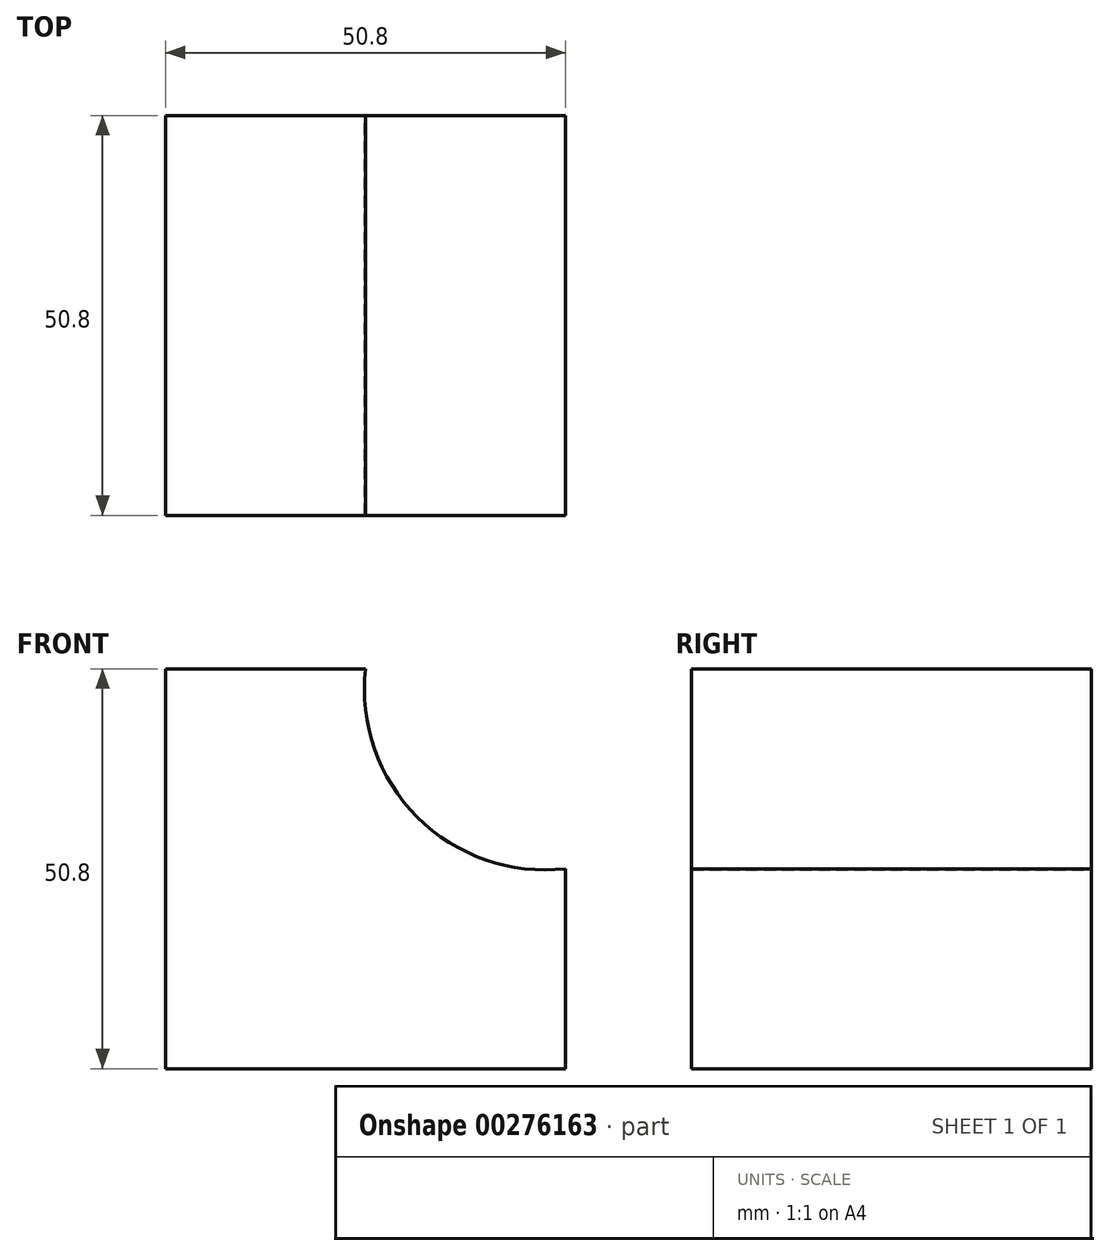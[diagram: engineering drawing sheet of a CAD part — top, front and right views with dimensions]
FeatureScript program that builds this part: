
annotation { "Feature Type Name" : "Feature", "Feature Type Description" : "" }
export const myFeature = defineFeature(function(context is Context, id is Id, definition is map)
    precondition{}
    {
        {
            var Q0;
            Q0=qCreatedBy(makeId("Front.planeOp"),FACE);
            var sketch = newSketch(context, id + "F0", { "sketchPlane" : qUnion([Q0])});
            skLineSegment(sketch, "E0", {"start": v(0, 0) * mm, "end": v(-50.8, 0) * mm});
            skLineSegment(sketch, "E1", {"start": v(-50.8, 0) * mm, "end": v(-50.8, 50.8) * mm});
            skLineSegment(sketch, "E2", {"start": v(-50.8, 50.8) * mm, "end": v(-25.4, 50.8) * mm});
            skLineSegment(sketch, "E3", {"start": v(0, 0) * mm, "end": v(0, 25.4) * mm});
            skArc(sketch, "E4", {"start": v(-25.4, 50.8) * mm, "mid": v(-18.83, 31.97) * mm, "end": v(0, 25.4) * mm});
            skSolve(sketch);
        }
        {
            var Q0;
            Q0 = qSketchRegion(id + "F0", true);
            extrude(context, id + "F1", {"entities" : qUnion([Q0]), "depth" : 50.8 * mm});
        }
    });
